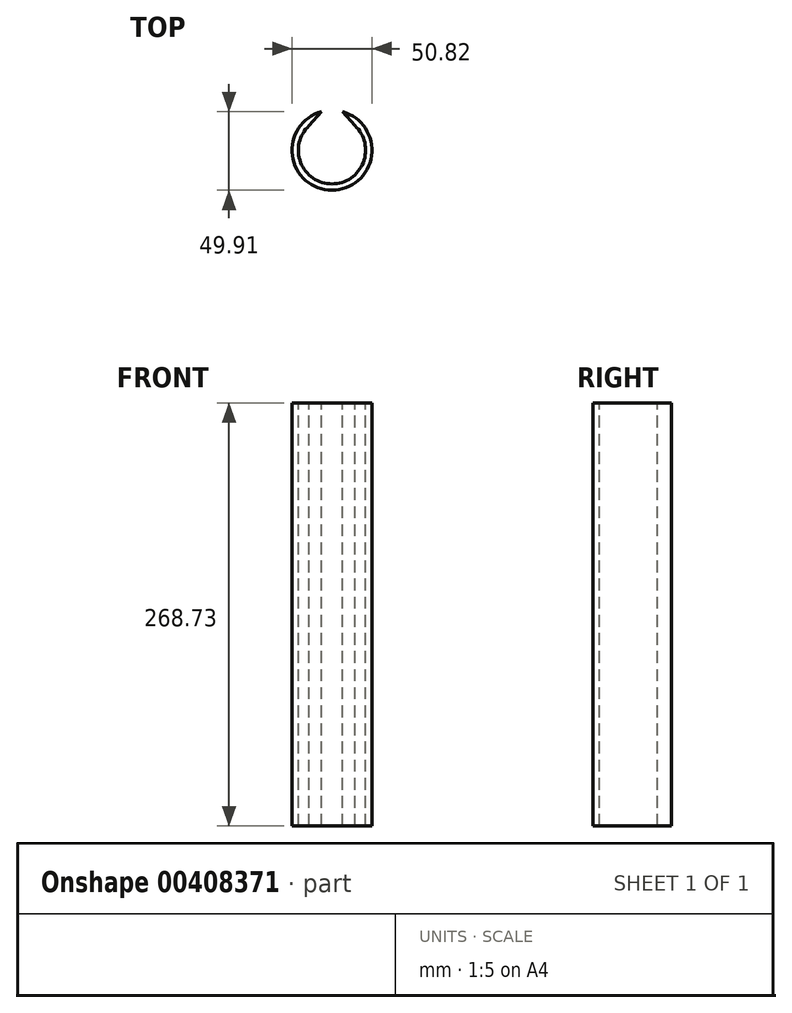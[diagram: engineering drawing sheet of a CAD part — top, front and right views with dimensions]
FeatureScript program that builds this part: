
annotation { "Feature Type Name" : "Feature", "Feature Type Description" : "" }
export const myFeature = defineFeature(function(context is Context, id is Id, definition is map)
    precondition{}
    {
        {
            var Q0;
            Q0=qCreatedBy(makeId("Top.planeOp"),FACE);
            var sketch = newSketch(context, id + "F0", { "sketchPlane" : qUnion([Q0])});
            skCircle(sketch, "E0", {"center": v(0, 0) * mm, "radius": 25.41 * mm});
            skSolve(sketch);
        }
        {
            var Q0;
            Q0 = qSketchRegion(id + "F0", true);
            extrude(context, id + "F1", {"entities" : qUnion([Q0]), "depth" : 268.73 * mm});
        }
        {
            var Q0;
            Q0=makeQuery(id+"F1.opExtrude","CAP_FACE",FACE,{"disambiguationData":[OSD([sQuery(id+"F0.wireOp",EDGE,"E0")])],"isStart":false});
            var sketch = newSketch(context, id + "F2", { "sketchPlane" : qUnion([Q0])});
            skCircle(sketch, "E1", {"center": v(0, 0) * mm, "radius": 21.36 * mm});
            skSolve(sketch);
        }
        {
            var Q0;
            Q0 = qSketchRegion(id + "F2", true);
            extrude(context, id + "F3", {"entities" : qUnion([Q0]), "operationType" : NewBodyOperationType.REMOVE, "oppositeDirection" : true, "depth" : 1270 * mm});
        }
        {
            var Q0;
            Q0=makeQuery(id+"F1.opExtrude","CAP_FACE",FACE,{"disambiguationData":[OSD([sQuery(id+"F0.wireOp",EDGE,"E0")])],"isStart":false});
            var sketch = newSketch(context, id + "F4", { "sketchPlane" : qUnion([Q0])});
            skLineSegment(sketch, "E2", {"start": v(-14.5, 15.69) * mm, "end": v(0, 32.18) * mm});
            skLineSegment(sketch, "E3", {"start": v(0, 32.18) * mm, "end": v(14.64, 15.69) * mm});
            skLineSegment(sketch, "E4", {"start": v(-14.5, 15.69) * mm, "end": v(14.64, 15.69) * mm});
            skSolve(sketch);
        }
        {
            var Q0;
            {var subQ3=sQuery(id+"F4.wireOp",EDGE,"E3");var subQ5=sQuery(id+"F4.wireOp",EDGE,"E4");var subQ6=makeQuery(id+"F4.imprint","INTERSECT",VERTEX,{"derivedFrom":[subQ3,subQ5]});Q0=makeQuery(id+"F4.imprint","IMPRINT",FACE,{"disambiguationData":[TD([[makeQuery(id+"F4.imprint","IMPRINT",EDGE,{"disambiguationData":[TD([[subQ6,1.0]])],"derivedFrom":subQ3}),-1.0]])]});}
            extrude(context, id + "F5", {"entities" : qUnion([Q0]), "operationType" : NewBodyOperationType.REMOVE, "oppositeDirection" : true, "depth" : 142240 * mm});
        }
    });
